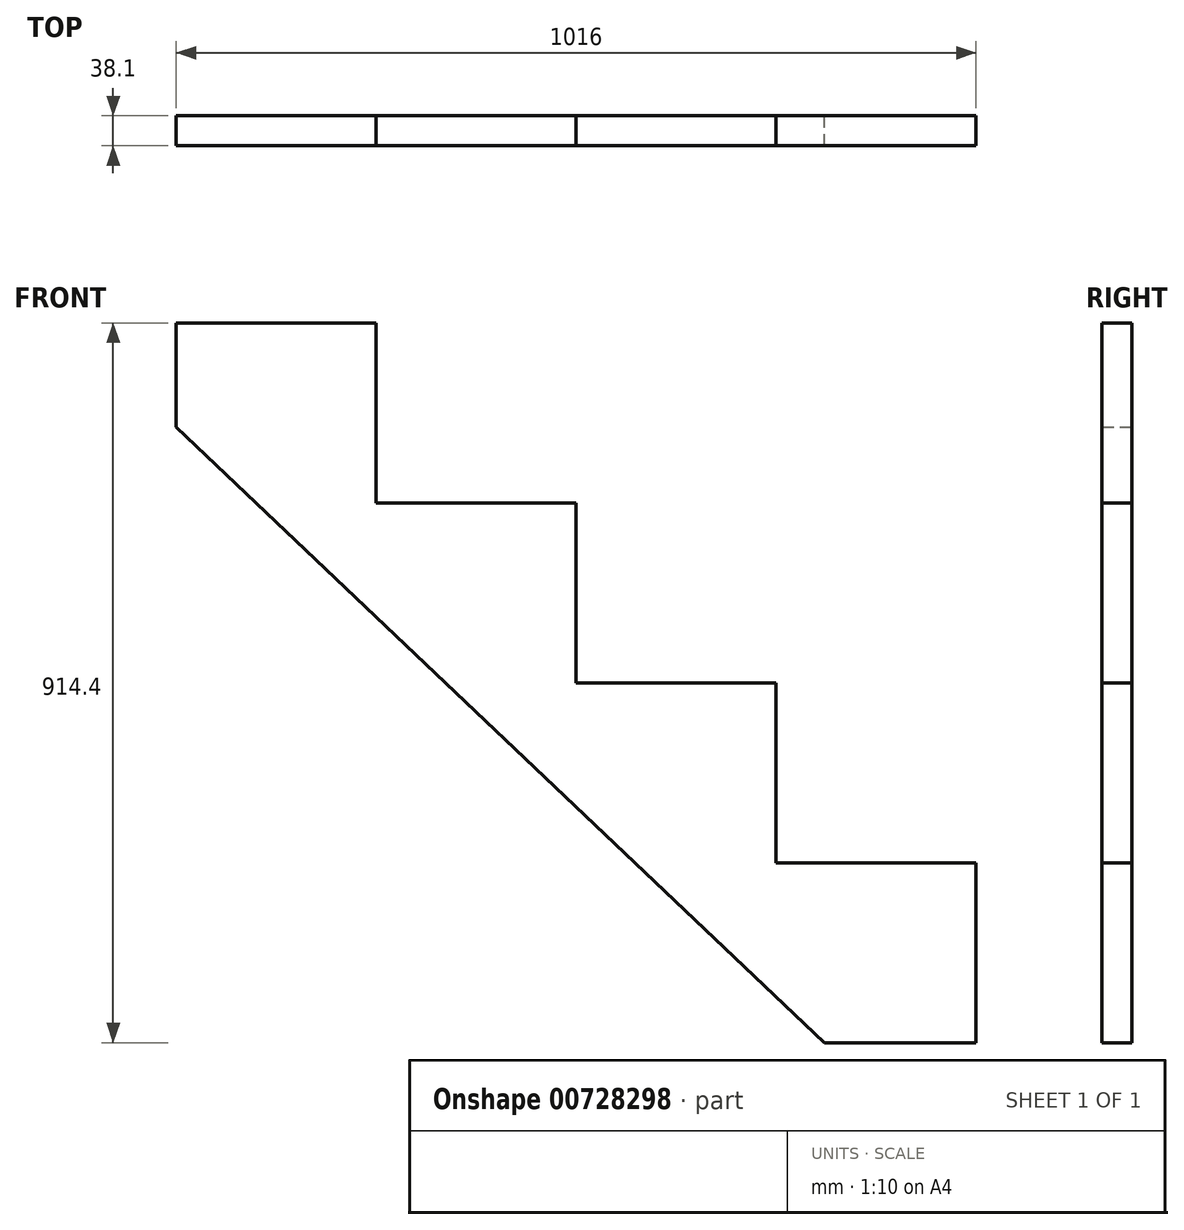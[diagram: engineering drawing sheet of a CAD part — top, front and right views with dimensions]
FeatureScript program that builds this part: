
annotation { "Feature Type Name" : "Feature", "Feature Type Description" : "" }
export const myFeature = defineFeature(function(context is Context, id is Id, definition is map)
    precondition{}
    {
        {
            var Q0;
            Q0=qCreatedBy(makeId("Front.planeOp"),FACE);
            var sketch = newSketch(context, id + "F0", { "sketchPlane" : qUnion([Q0])});
            skLineSegment(sketch, "E0", {"start": v(0, 0) * mm, "end": v(0, -228.6) * mm});
            skLineSegment(sketch, "E1", {"start": v(0, -228.6) * mm, "end": v(254, -228.6) * mm});
            skLineSegment(sketch, "E2", {"start": v(254, -228.6) * mm, "end": v(254, -457.2) * mm});
            skLineSegment(sketch, "E3", {"start": v(254, -457.2) * mm, "end": v(508, -457.2) * mm});
            skLineSegment(sketch, "E4", {"start": v(508, -457.2) * mm, "end": v(508, -685.8) * mm});
            skLineSegment(sketch, "E5", {"start": v(508, -685.8) * mm, "end": v(762, -685.8) * mm});
            skLineSegment(sketch, "E6", {"start": v(762, -685.8) * mm, "end": v(762, -914.4) * mm});
            skLineSegment(sketch, "E7", {"start": v(0, 0) * mm, "end": v(762, -685.8) * mm});
            skLineSegment(sketch, "E8", {"start": v(569.31, -914.4) * mm, "end": v(762, -914.4) * mm});
            skLineSegment(sketch, "E9", {"start": v(0, 0) * mm, "end": v(-254, 0) * mm});
            skLineSegment(sketch, "E10", {"start": v(-254, 0) * mm, "end": v(-254, -132.26) * mm});
            skLineSegment(sketch, "E11", {"start": v(-254, -132.26) * mm, "end": v(569.31, -914.4) * mm});
            skSolve(sketch);
        }
        {
            var Q0;
            Q0=makeQuery(id+"F0.imprint","IMPRINT",FACE,{"disambiguationData":[TD([[makeQuery(id+"F0.imprint","IMPRINT",EDGE,{"derivedFrom":sQuery(id+"F0.wireOp",EDGE,"E1")}),-1.0]])]});
            extrude(context, id + "F1", {"entities" : qUnion([Q0]), "depth" : 38.1 * mm, "offsetDistance" : 25.4 * mm});
        }
    });
